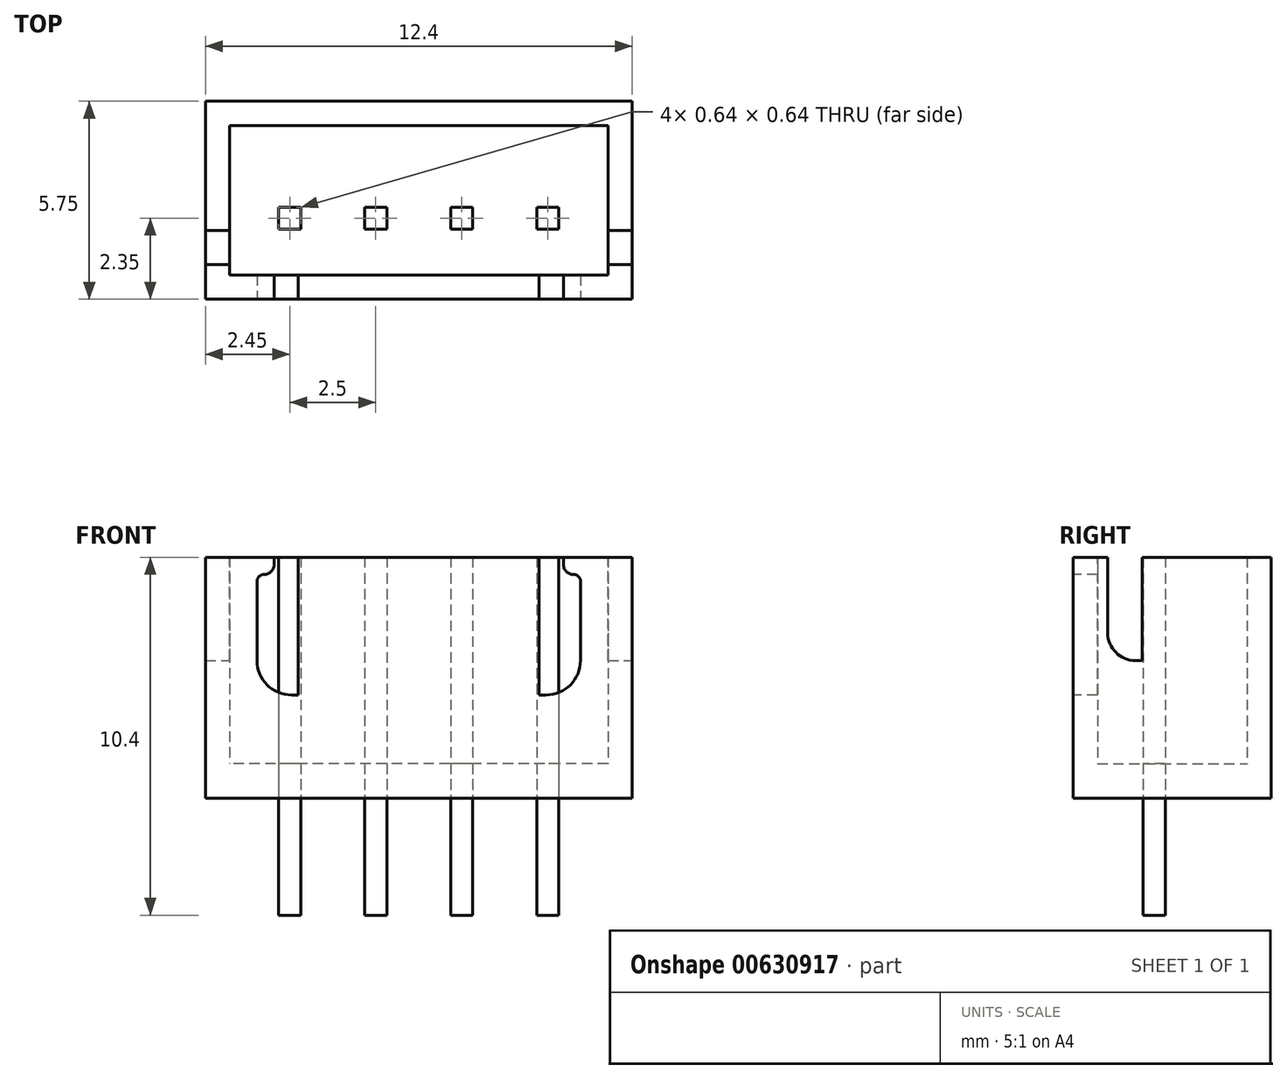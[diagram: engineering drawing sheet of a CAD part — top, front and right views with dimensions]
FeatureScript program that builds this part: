
annotation { "Feature Type Name" : "Feature", "Feature Type Description" : "" }
export const myFeature = defineFeature(function(context is Context, id is Id, definition is map)
    precondition{}
    {
        {
            var Q0;
            Q0=qCreatedBy(makeId("Top.planeOp"),FACE);
            var sketch = newSketch(context, id + "F0", { "sketchPlane" : qUnion([Q0])});
            skLineSegment(sketch, "E0.bottom", {"start": v(0, 0) * mm, "end": v(12.4, 0) * mm});
            skLineSegment(sketch, "E0.top", {"start": v(0, 5.75) * mm, "end": v(12.4, 5.75) * mm});
            skLineSegment(sketch, "E0.left", {"start": v(0, 0) * mm, "end": v(0, 5.75) * mm});
            skLineSegment(sketch, "E0.right", {"start": v(12.4, 0) * mm, "end": v(12.4, 5.75) * mm});
            skLineSegment(sketch, "E1.bottom", {"start": v(0.7, 5.05) * mm, "end": v(11.7, 5.05) * mm});
            skLineSegment(sketch, "E1.top", {"start": v(0.7, 0.7) * mm, "end": v(11.7, 0.7) * mm});
            skLineSegment(sketch, "E1.left", {"start": v(0.7, 5.05) * mm, "end": v(0.7, 0.7) * mm});
            skLineSegment(sketch, "E1.right", {"start": v(11.7, 5.05) * mm, "end": v(11.7, 0.7) * mm});
            skLineSegment(sketch, "E2.bottom", {"start": v(2.77, 2.67) * mm, "end": v(2.13, 2.67) * mm});
            skLineSegment(sketch, "E2.top", {"start": v(2.77, 2.03) * mm, "end": v(2.13, 2.03) * mm});
            skLineSegment(sketch, "E2.left", {"start": v(2.77, 2.67) * mm, "end": v(2.77, 2.03) * mm});
            skLineSegment(sketch, "E2.right", {"start": v(2.13, 2.67) * mm, "end": v(2.13, 2.03) * mm});
            skPoint(sketch, "E2.middle", {"position": v(2.45, 2.35) * mm});
            skLineSegment(sketch, "E3.1.0.0", {"start": v(5.27, 2.67) * mm, "end": v(4.63, 2.67) * mm});
            skPoint(sketch, "E3.1.0.1", {"position": v(4.95, 2.35) * mm});
            skLineSegment(sketch, "E3.1.0.2", {"start": v(5.27, 2.67) * mm, "end": v(5.27, 2.03) * mm});
            skLineSegment(sketch, "E3.1.0.3", {"start": v(5.27, 2.03) * mm, "end": v(4.63, 2.03) * mm});
            skLineSegment(sketch, "E3.1.0.4", {"start": v(4.63, 2.67) * mm, "end": v(4.63, 2.03) * mm});
            skLineSegment(sketch, "E3.2.0.0", {"start": v(7.77, 2.67) * mm, "end": v(7.13, 2.67) * mm});
            skPoint(sketch, "E3.2.0.1", {"position": v(7.45, 2.35) * mm});
            skLineSegment(sketch, "E3.2.0.2", {"start": v(7.77, 2.67) * mm, "end": v(7.77, 2.03) * mm});
            skLineSegment(sketch, "E3.2.0.3", {"start": v(7.77, 2.03) * mm, "end": v(7.13, 2.03) * mm});
            skLineSegment(sketch, "E3.2.0.4", {"start": v(7.13, 2.67) * mm, "end": v(7.13, 2.03) * mm});
            skLineSegment(sketch, "E3.3.0.0", {"start": v(10.27, 2.67) * mm, "end": v(9.63, 2.67) * mm});
            skPoint(sketch, "E3.3.0.1", {"position": v(9.95, 2.35) * mm});
            skLineSegment(sketch, "E3.3.0.2", {"start": v(10.27, 2.67) * mm, "end": v(10.27, 2.03) * mm});
            skLineSegment(sketch, "E3.3.0.3", {"start": v(10.27, 2.03) * mm, "end": v(9.63, 2.03) * mm});
            skLineSegment(sketch, "E3.3.0.4", {"start": v(9.63, 2.67) * mm, "end": v(9.63, 2.03) * mm});
            skLineSegment(sketch, "E3.direction1", {"start": v(2.13, 2.03) * mm, "end": v(4.63, 2.03) * mm, "construction": true});
            skSolve(sketch);
        }
        {
            var Q0;
            Q0=makeQuery(id+"F0.imprint","IMPRINT",FACE,{"disambiguationData":[TD([[makeQuery(id+"F0.imprint","IMPRINT",EDGE,{"derivedFrom":sQuery(id+"F0.wireOp",EDGE,"E0.bottom")}),1.0]])]});
            var Q1;
            Q1=makeQuery(id+"F0.imprint","IMPRINT",FACE,{"disambiguationData":[TD([[makeQuery(id+"F0.imprint","IMPRINT",EDGE,{"derivedFrom":sQuery(id+"F0.wireOp",EDGE,"E1.bottom")}),-1.0]])]});
            extrude(context, id + "F1", {"entities" : qUnion([Q0, Q1]), "depth" : 1 * mm});
        }
        {
            var Q0;
            Q0=makeQuery(id+"F0.imprint","IMPRINT",FACE,{"disambiguationData":[TD([[makeQuery(id+"F0.imprint","IMPRINT",EDGE,{"derivedFrom":sQuery(id+"F0.wireOp",EDGE,"E0.bottom")}),1.0]])]});
            extrude(context, id + "F2", {"entities" : qUnion([Q0]), "operationType" : NewBodyOperationType.ADD, "depth" : 7 * mm});
        }
        {
            var Q0;
            {var subQ0=sQuery(id+"F0.wireOp",EDGE,"E0.right");Q0=makeQuery(id+"F2.boolean.opBoolean","MERGE",FACE,{"derivedFrom":[makeQuery(id+"F1.opExtrude","SWEPT_FACE",FACE,{"disambiguationData":[OSD([subQ0])]}),makeQuery(id+"F2.opExtrude","SWEPT_FACE",FACE,{"disambiguationData":[OSD([subQ0])]})]});}
            var sketch = newSketch(context, id + "F3", { "sketchPlane" : qUnion([Q0])});
            skLineSegment(sketch, "E4", {"start": v(1, 7) * mm, "end": v(1, 4.8) * mm});
            skLineSegment(sketch, "E5", {"start": v(2, 4) * mm, "end": v(2, 7) * mm});
            skLineSegment(sketch, "E6", {"start": v(2, 7) * mm, "end": v(1, 7) * mm});
            skLineSegment(sketch, "E7", {"start": v(1.8, 4) * mm, "end": v(2, 4) * mm});
            skPoint(sketch, "E8.visualSharp", {"position": v(1, 4) * mm});
            skArc(sketch, "E8.filletArc", {"start": v(1, 4.8) * mm, "mid": v(1.23, 4.23) * mm, "end": v(1.8, 4) * mm});
            skSolve(sketch);
        }
        {
            var Q0;
            Q0=makeQuery(id+"F3.imprint","IMPRINT",FACE,{"disambiguationData":[TD([[makeQuery(id+"F3.imprint","IMPRINT",EDGE,{"derivedFrom":sQuery(id+"F3.wireOp",EDGE,"E4")}),1.0]])]});
            extrude(context, id + "F4", {"entities" : qUnion([Q0]), "operationType" : NewBodyOperationType.REMOVE, "oppositeDirection" : true, "depth" : 12.5 * mm});
        }
        {
            var Q0;
            {var subQ0=sQuery(id+"F0.wireOp",EDGE,"E0.bottom");Q0=makeQuery(id+"F2.boolean.opBoolean","MERGE",FACE,{"derivedFrom":[makeQuery(id+"F1.opExtrude","SWEPT_FACE",FACE,{"disambiguationData":[OSD([subQ0])]}),makeQuery(id+"F2.opExtrude","SWEPT_FACE",FACE,{"disambiguationData":[OSD([subQ0])]})]});}
            var sketch = newSketch(context, id + "F5", { "sketchPlane" : qUnion([Q0])});
            skLineSegment(sketch, "E9", {"start": v(6.2, 7) * mm, "end": v(6.2, 0) * mm, "construction": true});
            skLineSegment(sketch, "E10", {"start": v(9.7, 7) * mm, "end": v(9.7, 3) * mm});
            skLineSegment(sketch, "E11", {"start": v(9.7, 3) * mm, "end": v(9.9, 3) * mm});
            skLineSegment(sketch, "E12", {"start": v(10.9, 4) * mm, "end": v(10.9, 6.3) * mm});
            skLineSegment(sketch, "E13", {"start": v(10.7, 6.5) * mm, "end": v(10.7, 6.5) * mm});
            skLineSegment(sketch, "E14", {"start": v(10.4, 6.8) * mm, "end": v(10.4, 7) * mm});
            skLineSegment(sketch, "E15", {"start": v(10.4, 7) * mm, "end": v(9.7, 7) * mm});
            skPoint(sketch, "E16.visualSharp", {"position": v(10.9, 3) * mm});
            skArc(sketch, "E16.filletArc", {"start": v(9.9, 3) * mm, "mid": v(10.6, 3.3) * mm, "end": v(10.9, 4) * mm});
            skPoint(sketch, "E17.visualSharp", {"position": v(10.9, 6.5) * mm});
            skArc(sketch, "E17.filletArc", {"start": v(10.9, 6.3) * mm, "mid": v(10.84, 6.44) * mm, "end": v(10.7, 6.5) * mm});
            skPoint(sketch, "E18.visualSharp", {"position": v(10.4, 6.5) * mm});
            skArc(sketch, "E18.filletArc", {"start": v(10.4, 6.8) * mm, "mid": v(10.49, 6.59) * mm, "end": v(10.7, 6.5) * mm});
            skLineSegment(sketch, "E19.MirrorCS", {"start": v(2.7, 7) * mm, "end": v(2.7, 3) * mm});
            skLineSegment(sketch, "E20.MirrorCS", {"start": v(2, 7) * mm, "end": v(2.7, 7) * mm});
            skLineSegment(sketch, "E21.MirrorCS", {"start": v(2, 6.8) * mm, "end": v(2, 7) * mm});
            skArc(sketch, "E22.MirrorCS", {"start": v(2, 6.8) * mm, "mid": v(1.91, 6.59) * mm, "end": v(1.7, 6.5) * mm});
            skArc(sketch, "E23.MirrorCS", {"start": v(1.5, 6.3) * mm, "mid": v(1.56, 6.44) * mm, "end": v(1.7, 6.5) * mm});
            skLineSegment(sketch, "E24.MirrorCS", {"start": v(1.5, 4) * mm, "end": v(1.5, 6.3) * mm});
            skArc(sketch, "E25.MirrorCS", {"start": v(2.5, 3) * mm, "mid": v(1.8, 3.3) * mm, "end": v(1.5, 4) * mm});
            skLineSegment(sketch, "E26.MirrorCS", {"start": v(2.7, 3) * mm, "end": v(2.5, 3) * mm});
            skSolve(sketch);
        }
        {
            var Q0;
            Q0=makeQuery(id+"F5.imprint","IMPRINT",FACE,{"disambiguationData":[TD([[makeQuery(id+"F5.imprint","IMPRINT",EDGE,{"derivedFrom":sQuery(id+"F5.wireOp",EDGE,"E19.MirrorCS")}),-1.0]])]});
            var Q1;
            Q1=makeQuery(id+"F5.imprint","IMPRINT",FACE,{"disambiguationData":[TD([[makeQuery(id+"F5.imprint","IMPRINT",EDGE,{"derivedFrom":sQuery(id+"F5.wireOp",EDGE,"E10")}),1.0]])]});
            extrude(context, id + "F6", {"entities" : qUnion([Q0, Q1]), "operationType" : NewBodyOperationType.REMOVE, "oppositeDirection" : true, "depth" : 0.7 * mm});
        }
        {
            var Q0;
            Q0=makeQuery(id+"F0.imprint","IMPRINT",FACE,{"disambiguationData":[TD([[makeQuery(id+"F0.imprint","IMPRINT",EDGE,{"derivedFrom":sQuery(id+"F0.wireOp",EDGE,"E2.bottom")}),1.0]])]});
            var Q1;
            Q1=makeQuery(id+"F0.imprint","IMPRINT",FACE,{"disambiguationData":[TD([[makeQuery(id+"F0.imprint","IMPRINT",EDGE,{"derivedFrom":sQuery(id+"F0.wireOp",EDGE,"E3.1.0.0")}),1.0]])]});
            var Q2;
            Q2=makeQuery(id+"F0.imprint","IMPRINT",FACE,{"disambiguationData":[TD([[makeQuery(id+"F0.imprint","IMPRINT",EDGE,{"derivedFrom":sQuery(id+"F0.wireOp",EDGE,"E3.2.0.0")}),1.0]])]});
            var Q3;
            Q3=makeQuery(id+"F0.imprint","IMPRINT",FACE,{"disambiguationData":[TD([[makeQuery(id+"F0.imprint","IMPRINT",EDGE,{"derivedFrom":sQuery(id+"F0.wireOp",EDGE,"E3.3.0.0")}),1.0]])]});
            extrude(context, id + "F7", {"entities" : qUnion([Q0, Q1, Q2, Q3]), "depth" : 7 * mm, "hasSecondDirection" : true, "secondDirectionOppositeDirection" : true, "secondDirectionDepth" : 3.4 * mm});
        }
    });
